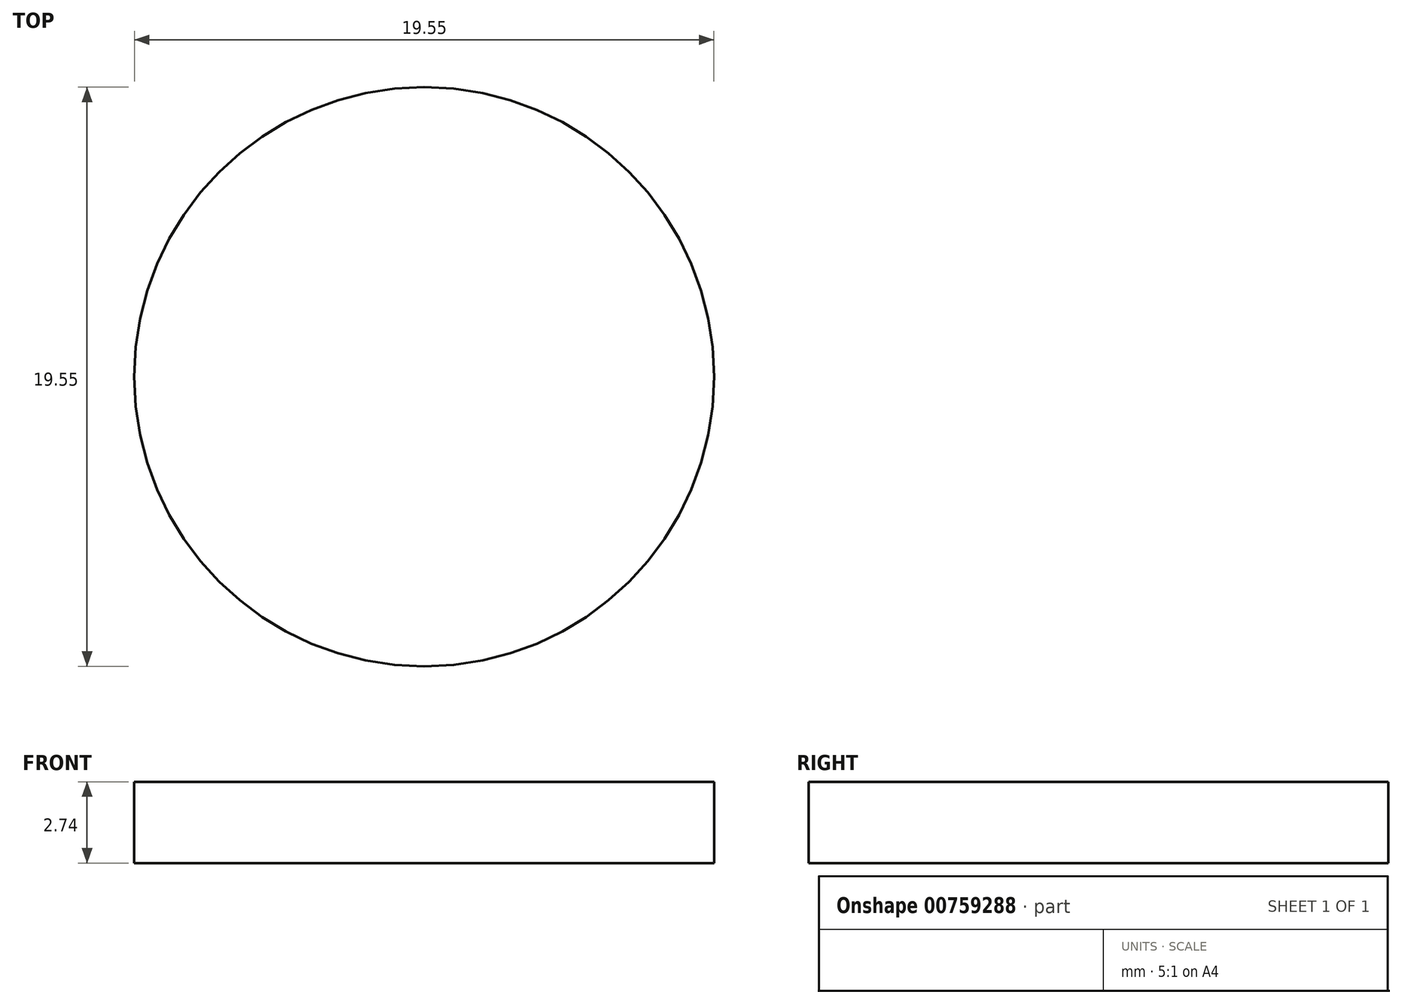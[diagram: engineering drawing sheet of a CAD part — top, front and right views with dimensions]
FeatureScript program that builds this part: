
annotation { "Feature Type Name" : "Feature", "Feature Type Description" : "" }
export const myFeature = defineFeature(function(context is Context, id is Id, definition is map)
    precondition{}
    {
        {
            var Q0;
            Q0=qCreatedBy(makeId("Top.planeOp"),FACE);
            var sketch = newSketch(context, id + "F0", { "sketchPlane" : qUnion([Q0])});
            skCircle(sketch, "E0", {"center": v(-132.46, -27.1) * mm, "radius": 9.78 * mm});
            skSolve(sketch);
        }
        {
            var Q0;
            Q0=makeQuery(id+"F0.imprint","IMPRINT",FACE,{"disambiguationData":[TD([[makeQuery(id+"F0.imprint","IMPRINT",EDGE,{"derivedFrom":sQuery(id+"F0.wireOp",EDGE,"E0")}),1.0]])]});
            extrude(context, id + "F1", {"entities" : qUnion([Q0]), "depth" : 2.74 * mm, "offsetDistance" : 25.4 * mm});
        }
    });
